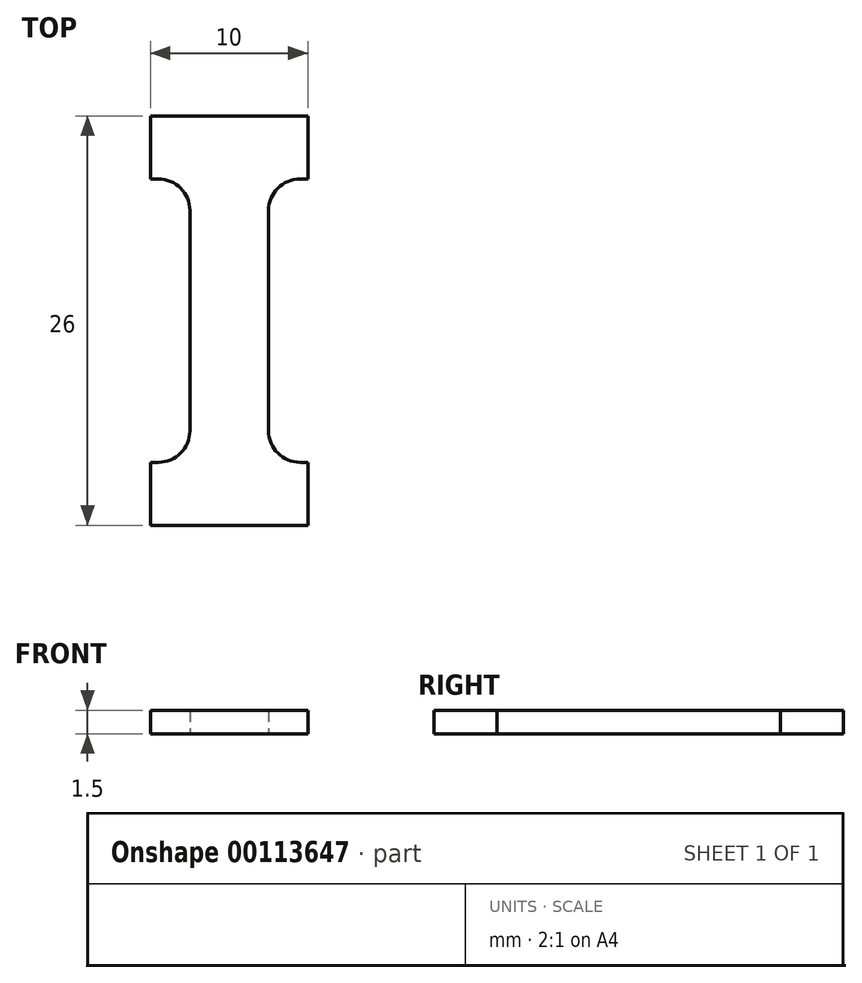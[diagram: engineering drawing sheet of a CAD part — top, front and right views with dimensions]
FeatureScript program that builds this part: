
annotation { "Feature Type Name" : "Feature", "Feature Type Description" : "" }
export const myFeature = defineFeature(function(context is Context, id is Id, definition is map)
    precondition{}
    {
        {
            var Q0;
            Q0=qCreatedBy(makeId("Top.planeOp"),FACE);
            var sketch = newSketch(context, id + "F0", { "sketchPlane" : qUnion([Q0])});
            skLineSegment(sketch, "E0", {"start": v(0, 0) * mm, "end": v(2.5, 0) * mm});
            skLineSegment(sketch, "E1", {"start": v(2.5, 0) * mm, "end": v(2.5, 7) * mm});
            skLineSegment(sketch, "E2", {"start": v(4.5, 9) * mm, "end": v(5, 9) * mm});
            skLineSegment(sketch, "E3", {"start": v(5, 9) * mm, "end": v(5, 13) * mm});
            skLineSegment(sketch, "E4", {"start": v(5, 13) * mm, "end": v(0, 13) * mm});
            skLineSegment(sketch, "E5", {"start": v(0, 13) * mm, "end": v(0, 0) * mm});
            skPoint(sketch, "E6.visualSharp", {"position": v(2.5, 9) * mm});
            skArc(sketch, "E6.filletArc", {"start": v(4.5, 9) * mm, "mid": v(3.09, 8.41) * mm, "end": v(2.5, 7) * mm});
            skLineSegment(sketch, "E7.MirrorCS", {"start": v(-5, 13) * mm, "end": v(0, 13) * mm});
            skLineSegment(sketch, "E8.MirrorCS", {"start": v(-5, 9) * mm, "end": v(-5, 13) * mm});
            skLineSegment(sketch, "E9.MirrorCS", {"start": v(-4.5, 9) * mm, "end": v(-5, 9) * mm});
            skArc(sketch, "E10.MirrorCS", {"start": v(-4.5, 9) * mm, "mid": v(-3.09, 8.41) * mm, "end": v(-2.5, 7) * mm});
            skLineSegment(sketch, "E11.MirrorCS", {"start": v(-2.5, 0) * mm, "end": v(-2.5, 7) * mm});
            skLineSegment(sketch, "E12.MirrorCS", {"start": v(0, 0) * mm, "end": v(-2.5, 0) * mm});
            skLineSegment(sketch, "E13.MirrorCS", {"start": v(4.5, -9) * mm, "end": v(5, -9) * mm});
            skLineSegment(sketch, "E14.MirrorCS", {"start": v(-4.5, -9) * mm, "end": v(-5, -9) * mm});
            skArc(sketch, "E15.MirrorCS", {"start": v(-4.5, -9) * mm, "mid": v(-3.09, -8.41) * mm, "end": v(-2.5, -7) * mm});
            skLineSegment(sketch, "E16.MirrorCS", {"start": v(5, -9) * mm, "end": v(5, -13) * mm});
            skLineSegment(sketch, "E17.MirrorCS", {"start": v(5, -13) * mm, "end": v(0, -13) * mm});
            skLineSegment(sketch, "E18.MirrorCS", {"start": v(-2.5, 0) * mm, "end": v(-2.5, -7) * mm});
            skLineSegment(sketch, "E19.MirrorCS", {"start": v(0, -13) * mm, "end": v(0, 0) * mm});
            skArc(sketch, "E20.MirrorCS", {"start": v(4.5, -9) * mm, "mid": v(3.09, -8.41) * mm, "end": v(2.5, -7) * mm});
            skLineSegment(sketch, "E21.MirrorCS", {"start": v(-5, -13) * mm, "end": v(0, -13) * mm});
            skLineSegment(sketch, "E22.MirrorCS", {"start": v(2.5, 0) * mm, "end": v(2.5, -7) * mm});
            skPoint(sketch, "E23.MirrorP", {"position": v(2.5, -9) * mm});
            skLineSegment(sketch, "E24.MirrorCS", {"start": v(-5, -9) * mm, "end": v(-5, -13) * mm});
            skSolve(sketch);
        }
        {
            var Q0;
            Q0=makeQuery(id+"F0.imprint","IMPRINT",FACE,{"disambiguationData":[TD([[makeQuery(id+"F0.imprint","IMPRINT",EDGE,{"derivedFrom":sQuery(id+"F0.wireOp",EDGE,"E5")}),-1.0]])]});
            var Q1;
            Q1=makeQuery(id+"F0.imprint","IMPRINT",FACE,{"disambiguationData":[TD([[makeQuery(id+"F0.imprint","IMPRINT",EDGE,{"derivedFrom":sQuery(id+"F0.wireOp",EDGE,"E1")}),1.0]])]});
            var Q2;
            Q2=makeQuery(id+"F0.imprint","IMPRINT",FACE,{"disambiguationData":[TD([[makeQuery(id+"F0.imprint","IMPRINT",EDGE,{"derivedFrom":sQuery(id+"F0.wireOp",EDGE,"E14.MirrorCS")}),1.0]])]});
            var Q3;
            Q3=makeQuery(id+"F0.imprint","IMPRINT",FACE,{"disambiguationData":[TD([[makeQuery(id+"F0.imprint","IMPRINT",EDGE,{"derivedFrom":sQuery(id+"F0.wireOp",EDGE,"E13.MirrorCS")}),-1.0]])]});
            extrude(context, id + "F1", {"entities" : qUnion([Q0, Q1, Q2, Q3]), "depth" : 1.5 * mm, "offsetDistance" : 25 * mm});
        }
    });
